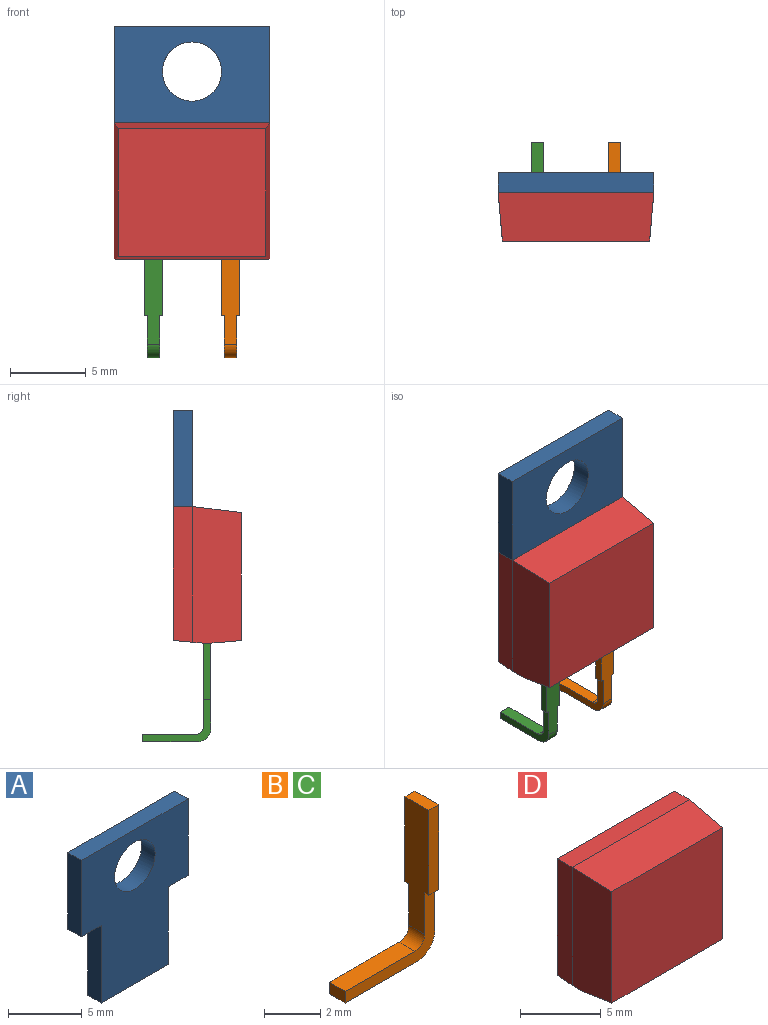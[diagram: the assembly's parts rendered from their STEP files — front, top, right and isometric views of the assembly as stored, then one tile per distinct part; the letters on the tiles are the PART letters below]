
ASSEMBLY  parts=4 mates=3
PART A: 11 faces, bbox 10.3x1.3x12.8 mm
  f0: plane 10.26x1.3mm, normal (0,0,1), area 13.3mm2, adj f1,f7,f8,f9
  f1: plane 6.35x1.3mm, normal (-1,0,0), area 8.3mm2, adj f0,f2,f8,f9
  f2: plane 1.91x1.3mm, normal (0,0,-1), area 2.5mm2, adj f1,f3,f8,f9
  f3: plane 6.45x1.3mm, normal (-1,0,0), area 8.4mm2, adj f2,f4,f8,f9
  f4: plane 6.44x1.3mm, normal (0,0,-1), area 8.4mm2, adj f3,f5,f8,f9
  f5: plane 6.45x1.3mm, normal (1,0,0), area 8.4mm2, adj f4,f6,f8,f9
  f6: plane 1.91x1.3mm, normal (0,0,-1), area 2.5mm2, adj f5,f7,f8,f9
  f7: plane 6.35x1.3mm, normal (1,0,0), area 8.3mm2, adj f0,f6,f8,f9
  f8: plane 12.8x10.26mm, normal (0,-1,0), area 94.8mm2, adj f0,f1,f2,f3,f4,f5,f6,f7
  f9: plane 12.8x10.26mm, normal (0,1,0), area 94.8mm2, adj f0,f1,f2,f3,f4,f5,f6,f7
  f10: cylinder r=1.95mm len=3.9mm, axis (0,1,0), area 15.9mm2, adj f8,f9
PART B: 14 faces, bbox 4.5x1.2x6.5 mm
  f0: plane 5.6x1.2mm, normal (1,0,0), area 6mm2, adj f6,f7,f8,f9,f10,f11,f12,f13
  f1: plane 5.5x1.2mm, normal (-1,0,0), area 5.9mm2, adj f2,f7,f8,f9,f10,f11,f12,f13
  f2: cylinder r=0.5mm len=0.8mm, axis (0,1,0), area 0.6mm2, adj f1,f3,f7,f8
  f3: plane 3.5x0.8mm, normal (0,0,1), area 2.8mm2, adj f2,f4,f7,f8
  f4: plane 0.8x0.5mm, normal (-1,0,0), area 0.4mm2, adj f3,f5,f7,f8
  f5: plane 3.6x0.8mm, normal (0,0,-1), area 2.9mm2, adj f4,f6,f7,f8
  f6: cylinder r=0.9mm len=0.9mm, axis (0,1,0), area 1.1mm2, adj f0,f5,f7,f8
  f7: plane 4.5x2.8mm, normal (0,-1,0), area 3.3mm2, adj f0,f1,f2,f3,f4,f5,f6,f9
  f8: plane 4.5x2.8mm, normal (0,1,0), area 3.3mm2, adj f0,f1,f2,f3,f4,f5,f6,f10
  f9: plane 0.5x0.2mm, normal (0,0,-1), area 0.1mm2, adj f0,f1,f7,f12
  f10: plane 0.5x0.2mm, normal (0,0,-1), area 0.1mm2, adj f0,f1,f8,f13
  f11: plane 1.2x0.5mm, normal (0,0,1), area 0.6mm2, adj f0,f1,f12,f13
  f12: plane 3.7x0.5mm, normal (0,-1,0), area 1.9mm2, adj f0,f1,f9,f11
  f13: plane 3.7x0.5mm, normal (0,1,0), area 1.9mm2, adj f0,f1,f10,f11
PART C: same geometry as B
PART D: 11 faces, bbox 10.3x4.5x9 mm
  f0: plane 8.94x1.3mm, normal (1,0,0), area 11.5mm2, adj f1,f5,f7,f9
  f1: plane 10.26x1.3mm, normal (0,0,1), area 13.3mm2, adj f0,f2,f5,f6
  f2: plane 8.94x1.3mm, normal (-1,0,0), area 11.5mm2, adj f1,f5,f8,f9
  f3: plane 10.14x0.5mm, normal (0,0,-1), area 5mm2, adj f7,f8,f9,f10
  f4: plane 9.7x8.43mm, normal (0,-1,0), area 81.8mm2, adj f6,f7,f8,f10
  f5: plane 10.26x8.83mm, normal (0,1,0), area 90.5mm2, adj f0,f1,f2,f9
  f6: plane 10.26x3.2mm, normal (0,-0.12,0.99), area 32.2mm2, adj f1,f4,f7,f8
  f7: plane 9x3.2mm, normal (1,-0.09,0), area 28.1mm2, adj f0,f3,f4,f6,f9,f10
  f8: plane 9x3.2mm, normal (-1,-0.09,0), area 28.1mm2, adj f2,f3,f4,f6,f9,f10
  f9: plane 10.26x2mm, normal (0,0.09,-1), area 20.6mm2, adj f0,f2,f3,f5,f7,f8
  f10: plane 10.05x2mm, normal (0,-0.09,-1), area 19.8mm2, adj f3,f4,f7,f8
PLACE A t=(30.13,0,-18.01)mm
PLACE B rot(axis=(0,0,-1),90deg) t=(2.54,-49.26,1.64)mm
PLACE C rot(axis=(0,0,-1),90deg) t=(-2.54,-49.26,1.64)mm
PLACE D t=(30.13,0,-3.36)mm
MATE fastened D.f3 <-> C.f11  axis (0,0,-1) through (0,-2,-12.36)mm
MATE fastened A.f2 <-> D.f1  axis (0,0,1) through (0,0,-3.36)mm
MATE fastened D.f3 <-> B.f11  axis (0,0,-1) through (0,-2,-12.36)mm
